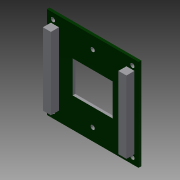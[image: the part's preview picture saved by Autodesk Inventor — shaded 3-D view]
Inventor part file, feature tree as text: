
AUTODESK INVENTOR PART (.ipt)
format: ipt  version: 2015 (Build 190159000, 159)  size: 138,752 bytes
history: native  units: in
note: dims shown in document units (in); Inventor stores cm internally (conversion verified against a paired STEP export)
features: extrude x2, sketch x2
ambient origin geometry x8: Origin, YZ Plane, XZ Plane, XY Plane, X Axis, Y Axis, Z Axis, Center Point
bodies: Solid1 (feature_tree)
feature tree (4):
  extrude  "Extrusion1"  Depth=2.25in
  extrude  "Extrusion4"  Depth=0.1in
  sketch  "Sketch1"  dims[d0=0.0646in d1=0.0in d2=2.25in]
  sketch  "Sketch4"  dims[d4=2.25in d21=0.1in d22=1.7717in d23=0.1969in d24=0.8858in d25=0.1969in d26=0.0in d27=0.1024in d28=0.15in d29=0.1024in d30=1.6535in d31=0.9843in d32=0.7874in]
